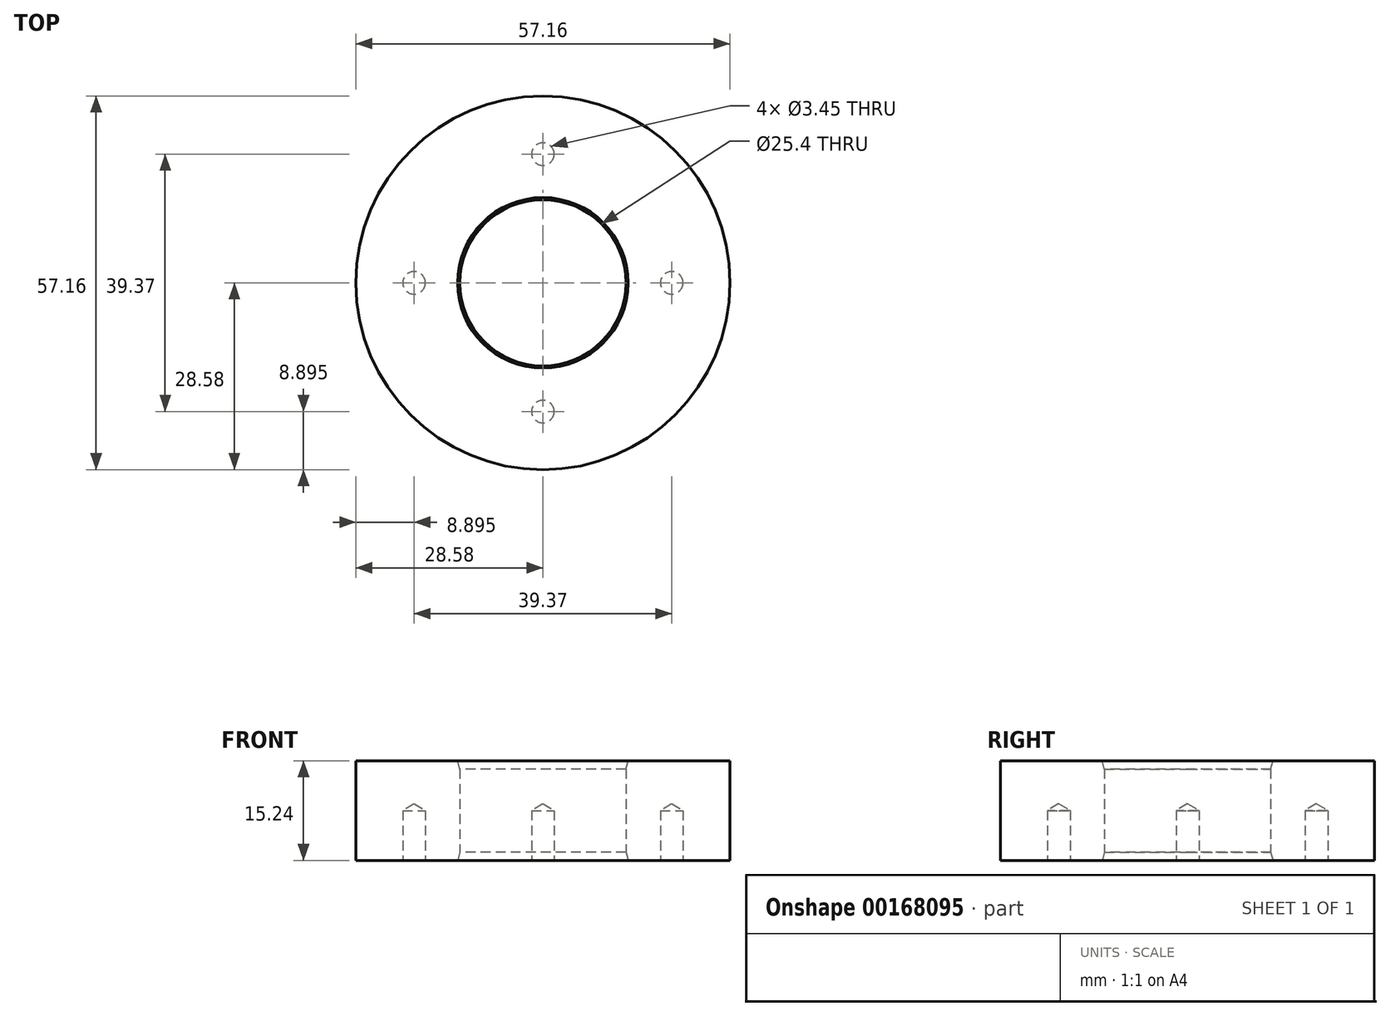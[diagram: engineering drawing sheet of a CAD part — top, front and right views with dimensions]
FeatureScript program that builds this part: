
annotation { "Feature Type Name" : "Feature", "Feature Type Description" : "" }
export const myFeature = defineFeature(function(context is Context, id is Id, definition is map)
    precondition{}
    {
        {
            var Q0;
            Q0=qCreatedBy(makeId("Top.planeOp"),FACE);
            var sketch = newSketch(context, id + "F0", { "sketchPlane" : qUnion([Q0])});
            skCircle(sketch, "E0", {"center": v(0, 0) * mm, "radius": 28.58 * mm});
            skCircle(sketch, "E1", {"center": v(0, 0) * mm, "radius": 12.7 * mm});
            skSolve(sketch);
        }
        {
            var Q0;
            Q0=qSketchRegion(id+"F0",true);
            extrude(context, id + "F1", {"entities" : qUnion([Q0]), "depth" : 15.24 * mm});
        }
        {
            var Q0;
            Q0=makeQuery(id+"F1.opExtrude","CAP_EDGE",EDGE,{"disambiguationData":[OSD([sQuery(id+"F0.wireOp",EDGE,"E1")])],"isStart":false});
            var Q1;
            Q1=makeQuery(id+"F1.opExtrude","CAP_EDGE",EDGE,{"disambiguationData":[OSD([sQuery(id+"F0.wireOp",EDGE,"E1")])],"isStart":true});
            chamfer(context, id + "F2", {"entities" : qUnion([Q0, Q1]), "chamferType" : ChamferType.OFFSET_ANGLE, "width" : 1.27 * mm, "oppositeDirection" : false, "angle" : 15 * degree, "tangentPropagation" : true});
        }
        {
            var Q0;
            Q0=makeQuery(id+"F1.opExtrude","CAP_FACE",FACE,{"disambiguationData":[OSD([sQuery(id+"F0.wireOp",EDGE,"E0"),sQuery(id+"F0.wireOp",EDGE,"E1")])],"isStart":true});
            var sketch = newSketch(context, id + "F3", { "sketchPlane" : qUnion([Q0])});
            skLineSegment(sketch, "E2", {"start": v(0, 0) * mm, "end": v(0, -16.51) * mm, "construction": true});
            skLineSegment(sketch, "E3", {"start": v(0, -16.51) * mm, "end": v(0, -22.86) * mm, "construction": true});
            skLineSegment(sketch, "E4", {"start": v(0, -22.86) * mm, "end": v(0, -16.51) * mm, "construction": true});
            skPoint(sketch, "E5", {"position": v(0, -19.69) * mm});
            skPoint(sketch, "E6.1.0", {"position": v(19.69, 0) * mm});
            skPoint(sketch, "E6.2.0", {"position": v(0, 19.69) * mm});
            skPoint(sketch, "E6.3.0", {"position": v(-19.69, 0) * mm});
            skPoint(sketch, "E6.center", {"position": v(0, 0) * mm});
            skSolve(sketch);
        }
        {
            var Q0;
            Q0=sQuery(id+"F3.wireOp",VERTEX,"E5");
            var Q1;
            Q1=sQuery(id+"F3.wireOp",VERTEX,"E6.3.0");
            var Q2;
            Q2=sQuery(id+"F3.wireOp",VERTEX,"E6.2.0");
            var Q3;
            Q3=sQuery(id+"F3.wireOp",VERTEX,"E6.1.0");
            var Q4;
            Q4=makeQuery(id+"F1.opExtrude","SWEPT_BODY",BODY,{"disambiguationData":[OSD([sQuery(id+"F0.wireOp",EDGE,"E0"),sQuery(id+"F0.wireOp",EDGE,"E1")])]});
            hole(context, id + "F4", {"style" : HoleStyle.SIMPLE, "endStyle" : HoleEndStyle.BLIND, "standardTappedOrClearance" : lookupTablePath({ "standard" : "ANSI", "engagement" : "75%", "pitch" : "32 tpi", "size" : "#8", "type" : "Tapped" }), "standardBlindInLast" : lookupTablePath({ "standard" : "ANSI", "engagement" : "75%", "pitch" : "32 tpi", "size" : "#8", "type" : "Tapped" }), "holeDiameter" : 3.45 * mm, "holeDepth" : 7.62 * mm, "locations" : qUnion([Q0, Q1, Q2, Q3]), "scope" : qUnion([Q4]), "majorDiameter" : 4.17 * mm});
        }
    });
